# Revit family: DBLTD_TheSenatorGroup_OffcStrg_Play_PrinterUnit
name_source: partatom
category: Furniture
revit_build: Autodesk Revit 2018 (Build: 20170223_1515(x64)
units: mm (PartAtom-declared; Revit-internal decimal feet)

## family parameters
Always vertical = Yes
Cut with Voids When Loaded = No
Room Calculation Point = No
Shared = Yes
Work Plane-Based = No

## types (2) — shared parameters
AssetType = Movable
BIMObjectName = TheSenatorGroup_OfficeStorage_Play_PrinterUnit
Category = Pr_40_30_78_57:Office storage units
DurationUnit = year
EdgeTrimMaterial = TheSenatorGroup_Play_MetalFrame_Black
Finish = HD Highland Oak, BH Beech, MP Maple, WH White, AT Autumn. WK Winter Oak, SO Strata Oak, MC Mocha, HW Hacienda White, DN Denim, LY Clay, LS Lemon Sorbet, LG Light Grey, CW Carini Walnut
FramesColour = Black, White, Totally Orange, Traffic Yellow, Anthracite, Pistachio
IfcExportAs = IfcFurnitureType
IfcExportType = STORAGE
Keynote = Pr_40_50_21_60
Manufacturer = The Senator Group
ManufacturerName = The Senator Group
ManufacturerURL = https://www.thesenatorgroup.com
Material = Metal, MFC
NBSDescription = Office storage
NBSReference = 45-35-80/360
Name = TheSenatorGroup_OfficeStorage_Play_PrinterUnit
OmniClassCode = 22-12 51 19
OmniClassTitle = Storage
OmniClassVersion = Table 22 2012-05-16
ProductInformation = https://www.thesenatorgroup.com
URL = https://www.thesenatorgroup.com
Uniclass2015Code = Pr_40_30_78_57
Uniclass2015Title = Office storage units
Uniclass2015Version = Products v1.9
Version = 1
WarrantyDescription = Senator warrants that its manufactured products are free from manufacturing defects - in materials or workmanship - for a period of ten (10) years on Senator Seating ranges; and fifteen (15) years on Senator Desking ranges
WarrantyDurationLabor = 15
WarrantyDurationParts = 15
WarrantyDurationUnit = Years
WarrantyGuarantorLabor = 15
WarrantyGuarantorParts = 15
zero-valued in all types: Cost

## per-type parameters (varying)
| type | Description | DimensionsHeight | DimensionsPlanSize | Model | ModelNumber | ModelReference | NominalDepth | NominalHeight | NominalLength | NominalWidth | Size |
| Printer Unit 1650mm(w) x 440mm(d) x 755mm(h) | 1650 mm x 440 mm Printer Unit | 755 | 1650 mm x 440 mm | PYPPSU16 | PYPPSU16 | 1650mm(w) x 440mm(d) x 775mm(h) | 440 mm | 755 mm | 1650 mm | 1650 mm | L 440mm x  W 1650mm x  H 755mm |
| Printer Unit with Screen 1686mm(w) x 600mm(d) x 1250mm(h) | 1686 mm x 600 mm Printer Unit with Screen | 1250 | 1686 mm x 600 mm | PYPPSU16 + PYPUFS16 | PYPPSU16 + PYPUFS16 | 1686mm(w) x 600mm(d) x 1250mm(h) | 600 mm  [stored 1.9685 ft] | 1250 mm  [stored 4.10105 ft] | 1686 mm  [stored 5.5315 ft] | 1686 mm  [stored 5.5315 ft] | L 600mm x  W 1686mm x  H 1250mm |

note: [stored X ft] marks values corroborated as IEEE doubles in the binary element streams (Revit-internal decimal feet)

## geometry (parser evidence)
native form markers: Sweep x8
no freeform markers — native parametric forms only
